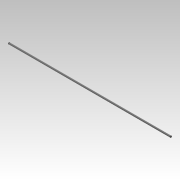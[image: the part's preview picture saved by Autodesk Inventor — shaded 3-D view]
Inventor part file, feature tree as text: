
AUTODESK INVENTOR PART (.ipt)
format: ipt  version: 2020 (Build 240168000, 168)  size: 84,992 bytes
history: native  units: mm
features: revolve x1, chamfer x1, sketch x1
ambient origin geometry x8: Origin, YZ Plane, XZ Plane, XY Plane, X Axis, Y Axis, Z Axis, Center Point
bodies: Solid1 (feature_tree)
feature tree (3):
  revolve  "Revolution1"  [1 undecoded]
  chamfer  "Chamfer1"  Distance=200.0mm
  sketch  "Sketch1"  dims[d0=0.5mm d1=1.0mm d2=200.0mm d3=90.0deg d4=0.25mm d5=2.0mm d6=45.0deg]
note: 1 required parameter value undecoded (feature->parameter linkage not recoverable at this tier; creation-order binding heuristic only, values carry confidence <= 0.55)
